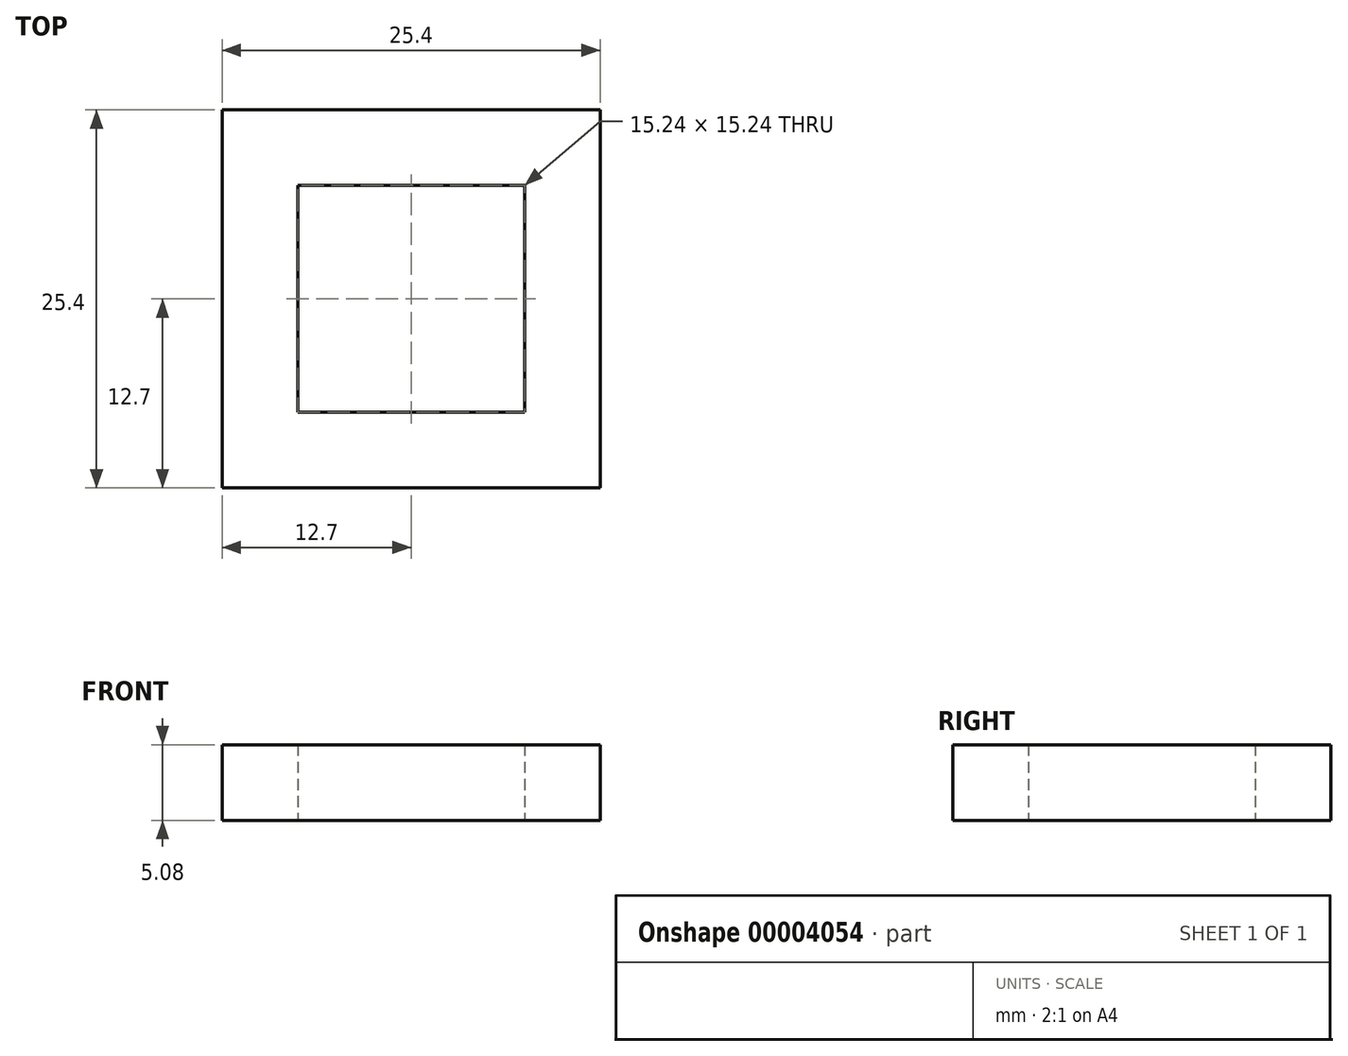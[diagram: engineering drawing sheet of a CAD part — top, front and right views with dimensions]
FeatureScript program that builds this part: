
annotation { "Feature Type Name" : "Feature", "Feature Type Description" : "" }
export const myFeature = defineFeature(function(context is Context, id is Id, definition is map)
    precondition{}
    {
        {
            var Q0;
            Q0=qCreatedBy(makeId("Top.planeOp"),FACE);
            var sketch = newSketch(context, id + "F0", { "sketchPlane" : qUnion([Q0])});
            skLineSegment(sketch, "E0.rect.bottom", {"start": v(12.7, -12.7) * mm, "end": v(-12.7, -12.7) * mm});
            skLineSegment(sketch, "E0.rect.top", {"start": v(12.7, 12.7) * mm, "end": v(-12.7, 12.7) * mm});
            skLineSegment(sketch, "E0.rect.left", {"start": v(12.7, -12.7) * mm, "end": v(12.7, 12.7) * mm});
            skLineSegment(sketch, "E0.rect.right", {"start": v(-12.7, -12.7) * mm, "end": v(-12.7, 12.7) * mm});
            skPoint(sketch, "E0.rect.middle", {"position": v(0, 0) * mm});
            skLineSegment(sketch, "E1.0", {"start": v(7.62, 7.62) * mm, "end": v(-7.62, 7.62) * mm});
            skLineSegment(sketch, "E1.1", {"start": v(7.62, -7.62) * mm, "end": v(7.62, 7.62) * mm});
            skLineSegment(sketch, "E1.2", {"start": v(7.62, -7.62) * mm, "end": v(-7.62, -7.62) * mm});
            skLineSegment(sketch, "E1.3", {"start": v(-7.62, -7.62) * mm, "end": v(-7.62, 7.62) * mm});
            skSolve(sketch);
        }
        {
            var Q0;
            Q0 = qSketchRegion(id + "F0", true);
            extrude(context, id + "F1", {"entities" : qUnion([Q0]), "depth" : 5.08 * mm});
        }
    });
